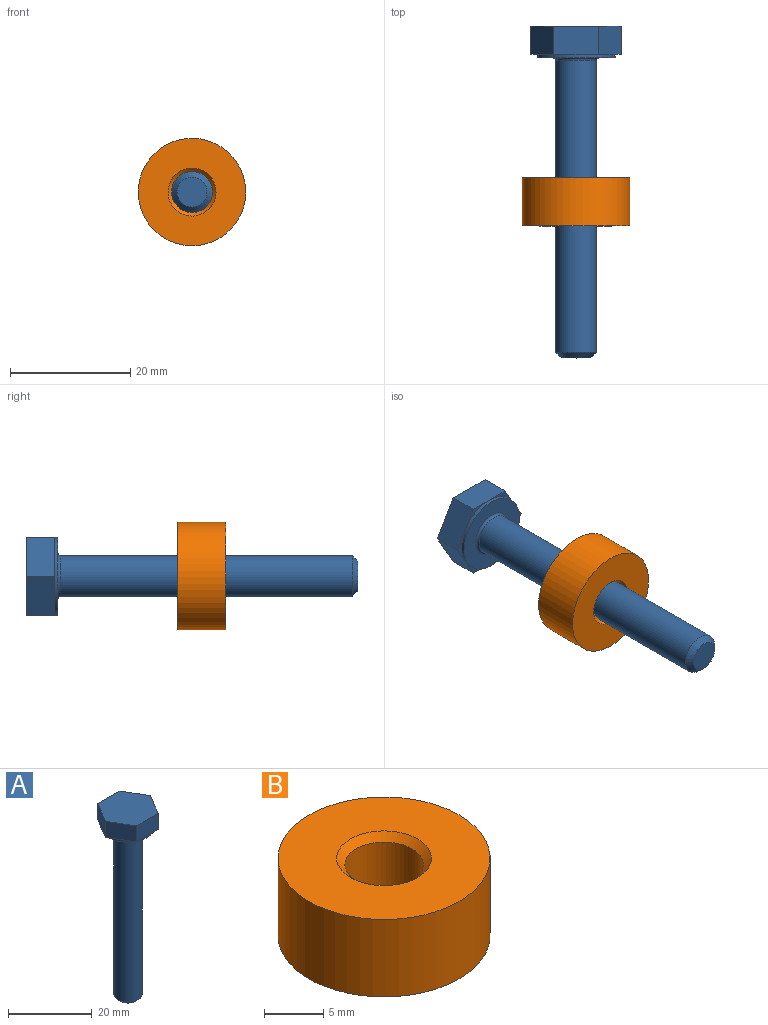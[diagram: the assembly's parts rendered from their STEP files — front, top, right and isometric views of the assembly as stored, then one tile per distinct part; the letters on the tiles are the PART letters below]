
ASSEMBLY  parts=2 mates=2
PART A: 19 faces, bbox 15x13x55.3 mm
  f0: plane 6.5x4.7mm, normal (0.87,0.5,0), area 35.3mm2, adj f1,f5,f14,f16,f18
  f1: plane 6.5x4.7mm, normal (0.87,-0.5,0), area 35.3mm2, adj f0,f8,f14,f15,f18
  f2: torus R=3.81mm, axis (0,0,1), area 14.1mm2, adj f6,f7
  f3: cone r=2.91mm half-angle=45deg, axis (0,0,1), area 24.1mm2, adj f4,f6
  f4: plane 4.99x4.99mm, normal (0,0,-1), area 19.6mm2, adj f3
  f5: plane 5.63x3.25mm, normal (0,0,-1), area 2.3mm2, adj f0,f12,f16
  f6: cylinder r=3.42mm len=48.68mm, axis (0,0,-1), area 1044.6mm2, adj f2,f3
  f7: plane 13x13mm, normal (0,0,-1), area 87mm2, adj f2,f12
  f8: plane 7.51x4.7mm, normal (0,-1,0), area 35.3mm2, adj f1,f13,f15,f17,f18
  f9: plane 6.5x4.7mm, normal (-0.87,0.5,0), area 35.3mm2, adj f10,f11,f16,f17,f18
  f10: plane 5.63x3.25mm, normal (0,0,-1), area 2.3mm2, adj f9,f12,f16
  f11: plane 6.5x1.88mm, normal (0,0,-1), area 2.3mm2, adj f9,f12,f17
  f12: cylinder r=6.5mm len=13mm, axis (0,0,1), area 24.5mm2, adj f5,f7,f10,f11,f13,f14,f15
  f13: plane 5.63x3.25mm, normal (0,0,-1), area 2.3mm2, adj f8,f12,f17
  f14: plane 6.5x1.88mm, normal (0,0,-1), area 2.3mm2, adj f0,f1,f12
  f15: plane 5.63x3.25mm, normal (0,0,-1), area 2.3mm2, adj f1,f8,f12
  f16: plane 7.51x4.7mm, normal (0,1,0), area 35.3mm2, adj f0,f5,f9,f10,f18
  f17: plane 6.5x4.7mm, normal (-0.87,-0.5,0), area 35.3mm2, adj f8,f9,f11,f13,f18
  f18: plane 15.01x13mm, normal (0,0,1), area 146.4mm2, adj f0,f1,f8,f9,f16,f17
PART B: 6 faces, bbox 17.9x17.9x8 mm
  f0: cone r=4mm half-angle=45deg, axis (0,0,-1), area 22mm2, adj f2,f3
  f1: cone r=3.32mm half-angle=45deg, axis (0,0,1), area 22mm2, adj f2,f4
  f2: cylinder r=3.32mm len=6.65mm, axis (0,0,1), area 138.8mm2, adj f0,f1
  f3: plane 17.91x17.91mm, normal (0,0,-1), area 201.5mm2, adj f0,f5
  f4: plane 17.91x17.91mm, normal (0,0,1), area 201.5mm2, adj f1,f5
  f5: cylinder r=8.95mm len=17.91mm, axis (0,0,1), area 450mm2, adj f3,f4
PLACE A rot(axis=(-1,0,0),90deg) t=(0,50,0)mm
PLACE B rot(axis=(0.08,-0.7,0.7),171deg) t=(0,26,0)mm
MATE parallel B.f5 <-> A.f2  axis (0,-1,0) through (0,30,0)mm
MATE cylindrical A.f2 <-> B.f5  axis (0,-1,0) through (0,0,0)mm
